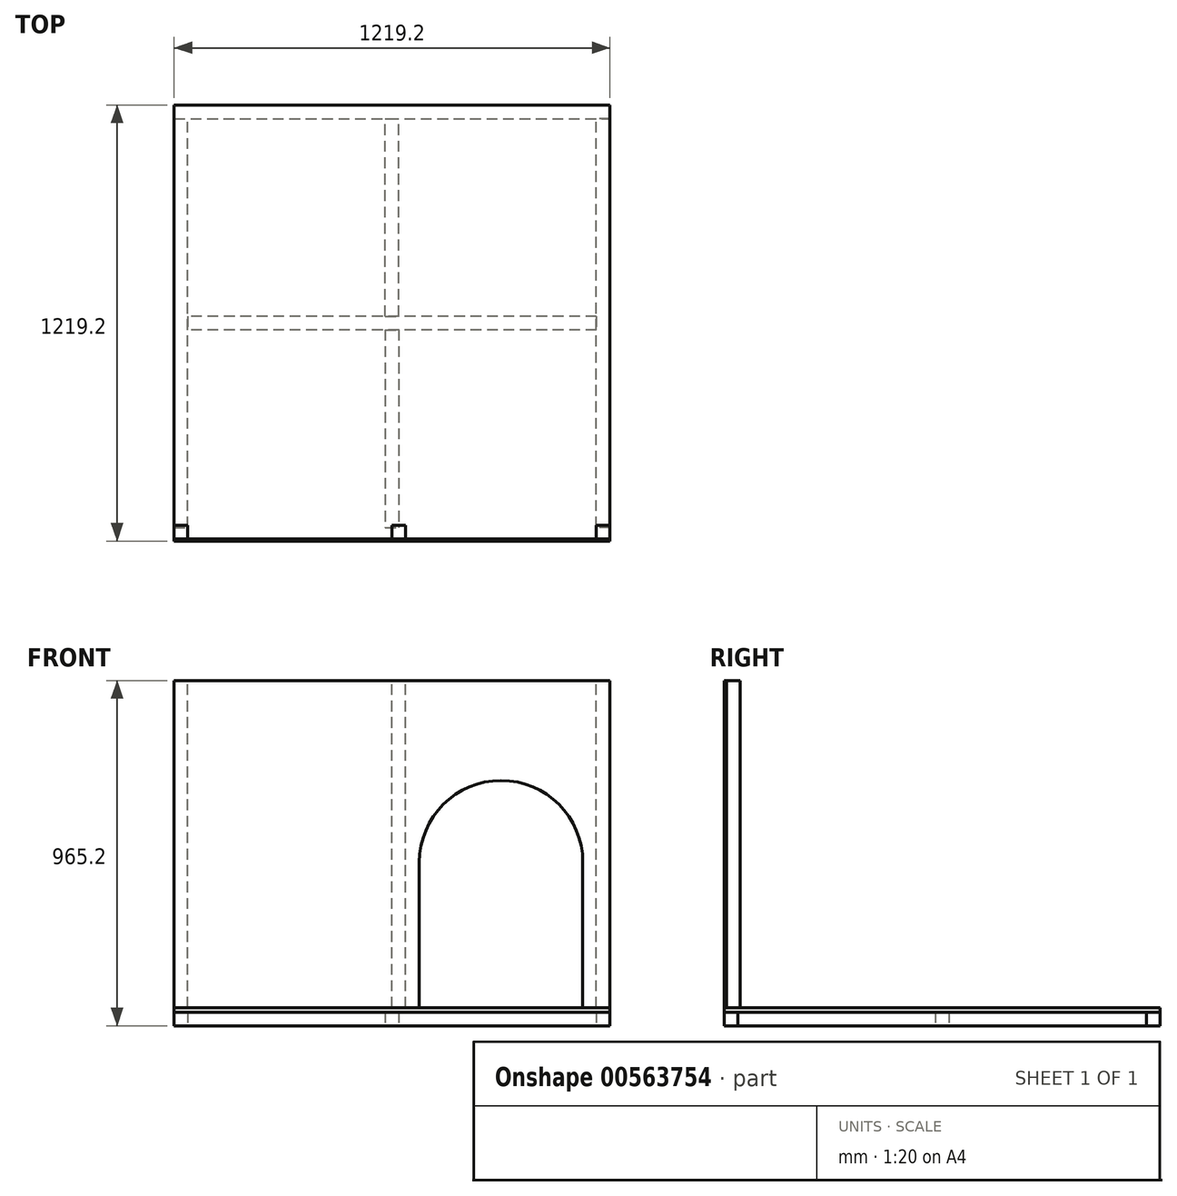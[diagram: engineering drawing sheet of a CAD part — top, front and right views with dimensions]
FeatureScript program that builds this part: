
annotation { "Feature Type Name" : "Feature", "Feature Type Description" : "" }
export const myFeature = defineFeature(function(context is Context, id is Id, definition is map)
    precondition{}
    {
        {
            var Q0;
            Q0=qCreatedBy(makeId("Top.planeOp"),FACE);
            var sketch = newSketch(context, id + "F0", { "sketchPlane" : qUnion([Q0])});
            skLineSegment(sketch, "E0.bottom", {"start": v(609.6, 609.6) * mm, "end": v(-609.6, 609.6) * mm, "construction": true});
            skLineSegment(sketch, "E0.top", {"start": v(609.6, -609.6) * mm, "end": v(-609.6, -609.6) * mm, "construction": true});
            skLineSegment(sketch, "E0.left", {"start": v(609.6, 609.6) * mm, "end": v(609.6, -609.6) * mm, "construction": true});
            skLineSegment(sketch, "E0.right", {"start": v(-609.6, 609.6) * mm, "end": v(-609.6, -609.6) * mm, "construction": true});
            skPoint(sketch, "E0.middle", {"position": v(0, 0) * mm});
            skSolve(sketch);
        }
        {
            var Q0;
            Q0=qCreatedBy(makeId("Top.planeOp"),FACE);
            var sketch = newSketch(context, id + "F1", { "sketchPlane" : qUnion([Q0])});
            skPoint(sketch, "E1.0", {"position": v(-609.6, -609.6) * mm});
            skLineSegment(sketch, "E2.bottom", {"start": v(-609.6, -609.6) * mm, "end": v(609.6, -609.6) * mm});
            skLineSegment(sketch, "E2.top", {"start": v(-609.6, -571.5) * mm, "end": v(609.6, -571.5) * mm});
            skLineSegment(sketch, "E2.left", {"start": v(-609.6, -609.6) * mm, "end": v(-609.6, -571.5) * mm});
            skLineSegment(sketch, "E2.right", {"start": v(609.6, -609.6) * mm, "end": v(609.6, -571.5) * mm});
            skPoint(sketch, "E3.0", {"position": v(-609.6, 609.6) * mm});
            skLineSegment(sketch, "E4.bottom", {"start": v(-609.6, 609.6) * mm, "end": v(609.6, 609.6) * mm});
            skLineSegment(sketch, "E4.top", {"start": v(-609.6, 571.5) * mm, "end": v(609.6, 571.5) * mm});
            skLineSegment(sketch, "E4.left", {"start": v(-609.6, 609.6) * mm, "end": v(-609.6, 571.5) * mm});
            skLineSegment(sketch, "E4.right", {"start": v(609.6, 609.6) * mm, "end": v(609.6, 571.5) * mm});
            skLineSegment(sketch, "E5.bottom", {"start": v(571.5, 19.05) * mm, "end": v(-571.5, 19.05) * mm});
            skLineSegment(sketch, "E5.top", {"start": v(571.5, -19.05) * mm, "end": v(-571.5, -19.05) * mm});
            skLineSegment(sketch, "E5.left", {"start": v(571.5, 19.05) * mm, "end": v(571.5, -19.05) * mm});
            skLineSegment(sketch, "E5.right", {"start": v(-571.5, 19.05) * mm, "end": v(-571.5, -19.05) * mm});
            skPoint(sketch, "E5.middle", {"position": v(0, 0) * mm});
            skSolve(sketch);
        }
        {
            var Q0;
            Q0 = qSketchRegion(id + "F1", true);
            extrude(context, id + "F2", {"entities" : qUnion([Q0]), "depth" : 38.1 * mm, "offsetDistance" : 25.4 * mm});
        }
        {
            var Q0;
            Q0=qCreatedBy(makeId("Top.planeOp"),FACE);
            var sketch = newSketch(context, id + "F3", { "sketchPlane" : qUnion([Q0])});
            skPoint(sketch, "E6.0", {"position": v(609.6, 0) * mm});
            skPoint(sketch, "E7.0", {"position": v(-609.6, 0) * mm});
            skPoint(sketch, "E8.0", {"position": v(609.6, -609.6) * mm});
            skLineSegment(sketch, "E9", {"start": v(609.6, -609.6) * mm, "end": v(609.6, -571.5) * mm, "construction": true});
            skLineSegment(sketch, "E10.bottom", {"start": v(609.6, -571.5) * mm, "end": v(571.5, -571.5) * mm});
            skLineSegment(sketch, "E10.top", {"start": v(609.6, 571.5) * mm, "end": v(571.5, 571.5) * mm});
            skLineSegment(sketch, "E10.left", {"start": v(609.6, -571.5) * mm, "end": v(609.6, 571.5) * mm});
            skLineSegment(sketch, "E10.right", {"start": v(571.5, -571.5) * mm, "end": v(571.5, 571.5) * mm});
            skLineSegment(sketch, "E11.MirrorCS", {"start": v(-571.5, -571.5) * mm, "end": v(-571.5, 571.5) * mm});
            skLineSegment(sketch, "E12.MirrorCS", {"start": v(-609.6, -571.5) * mm, "end": v(-609.6, 571.5) * mm});
            skLineSegment(sketch, "E13.MirrorCS", {"start": v(-609.6, 571.5) * mm, "end": v(-571.5, 571.5) * mm});
            skLineSegment(sketch, "E14.MirrorCS", {"start": v(-609.6, -571.5) * mm, "end": v(-571.5, -571.5) * mm});
            skSolve(sketch);
        }
        {
            var Q0;
            Q0 = qSketchRegion(id + "F3", true);
            extrude(context, id + "F4", {"entities" : qUnion([Q0]), "depth" : 38.1 * mm, "offsetDistance" : 25.4 * mm});
        }
        {
            var Q0;
            Q0=qCreatedBy(makeId("Top.planeOp"),FACE);
            var sketch = newSketch(context, id + "F5", { "sketchPlane" : qUnion([Q0])});
            skLineSegment(sketch, "E15", {"start": v(0, 19.05) * mm, "end": v(0, -19.05) * mm, "construction": true});
            skLineSegment(sketch, "E16.bottom", {"start": v(-19.05, 19.05) * mm, "end": v(19.05, 19.05) * mm});
            skLineSegment(sketch, "E16.top", {"start": v(-19.05, 571.5) * mm, "end": v(19.05, 571.5) * mm});
            skLineSegment(sketch, "E16.left", {"start": v(-19.05, 19.05) * mm, "end": v(-19.05, 571.5) * mm});
            skLineSegment(sketch, "E16.right", {"start": v(19.05, 19.05) * mm, "end": v(19.05, 571.5) * mm});
            skLineSegment(sketch, "E17.MirrorCS", {"start": v(19.05, -19.05) * mm, "end": v(19.05, -571.5) * mm});
            skLineSegment(sketch, "E18.MirrorCS", {"start": v(-19.05, -19.05) * mm, "end": v(-19.05, -571.5) * mm});
            skLineSegment(sketch, "E19.MirrorCS", {"start": v(-19.05, -19.05) * mm, "end": v(19.05, -19.05) * mm});
            skLineSegment(sketch, "E20.MirrorCS", {"start": v(-19.05, -571.5) * mm, "end": v(19.05, -571.5) * mm});
            skSolve(sketch);
        }
        {
            var Q0;
            Q0 = qSketchRegion(id + "F5", true);
            extrude(context, id + "F6", {"entities" : qUnion([Q0]), "depth" : 38.1 * mm, "offsetDistance" : 25.4 * mm});
        }
        {
            var Q0;
            Q0=makeQuery(id+"F2.opExtrude","CAP_FACE",FACE,{"disambiguationData":[OSD([sQuery(id+"F1.wireOp",EDGE,"E4.bottom"),sQuery(id+"F1.wireOp",EDGE,"E4.top"),sQuery(id+"F1.wireOp",EDGE,"E4.left"),sQuery(id+"F1.wireOp",EDGE,"E4.right")])],"isStart":false});
            var sketch = newSketch(context, id + "F7", { "sketchPlane" : qUnion([Q0])});
            skPoint(sketch, "E21.0", {"position": v(609.6, -609.6) * mm});
            skPoint(sketch, "E22.0", {"position": v(-609.6, 609.6) * mm});
            skLineSegment(sketch, "E23.bottom", {"start": v(609.6, -609.6) * mm, "end": v(-609.6, -609.6) * mm});
            skLineSegment(sketch, "E23.top", {"start": v(609.6, 609.6) * mm, "end": v(-609.6, 609.6) * mm});
            skLineSegment(sketch, "E23.left", {"start": v(609.6, -609.6) * mm, "end": v(609.6, 609.6) * mm});
            skLineSegment(sketch, "E23.right", {"start": v(-609.6, -609.6) * mm, "end": v(-609.6, 609.6) * mm});
            skSolve(sketch);
        }
        {
            var Q0;
            Q0 = qSketchRegion(id + "F7", true);
            extrude(context, id + "F8", {"entities" : qUnion([Q0]), "depth" : 12.7 * mm, "offsetDistance" : 25.4 * mm});
        }
        {
            var Q0;
            Q0=makeQuery(id+"F8.opExtrude","SWEPT_FACE",FACE,{"disambiguationData":[OSD([sQuery(id+"F7.wireOp",EDGE,"E23.bottom")])]});
            var sketch = newSketch(context, id + "F9", { "sketchPlane" : qUnion([Q0])});
            skPoint(sketch, "E24.0", {"position": v(-609.6, 50.8) * mm});
            skPoint(sketch, "E25.0", {"position": v(609.6, 50.8) * mm});
            skLineSegment(sketch, "E26.bottom", {"start": v(-609.6, 50.8) * mm, "end": v(609.6, 50.8) * mm});
            skLineSegment(sketch, "E26.top", {"start": v(-609.6, 965.2) * mm, "end": v(609.6, 965.2) * mm});
            skLineSegment(sketch, "E26.left", {"start": v(-609.6, 50.8) * mm, "end": v(-609.6, 965.2) * mm});
            skLineSegment(sketch, "E26.right", {"start": v(609.6, 50.8) * mm, "end": v(609.6, 965.2) * mm});
            skSolve(sketch);
        }
        {
            var Q0;
            Q0 = qSketchRegion(id + "F9", true);
            extrude(context, id + "F10", {"entities" : qUnion([Q0]), "oppositeDirection" : true, "depth" : 6.35 * mm, "offsetDistance" : 25.4 * mm});
        }
        {
            var Q0;
            Q0=makeQuery(id+"F10.boolean.opBoolean","MERGE",FACE,{"derivedFrom":[makeQuery(id+"F8.opExtrude","SWEPT_FACE",FACE,{"disambiguationData":[OSD([sQuery(id+"F7.wireOp",EDGE,"E23.bottom")])]}),makeQuery(id+"F10.opExtrude","CAP_FACE",FACE,{"disambiguationData":[OSD([sQuery(id+"F9.wireOp",EDGE,"E26.bottom"),sQuery(id+"F9.wireOp",EDGE,"E26.top"),sQuery(id+"F9.wireOp",EDGE,"E26.left"),sQuery(id+"F9.wireOp",EDGE,"E26.right")])],"isStart":true})]});
            var sketch = newSketch(context, id + "F11", { "sketchPlane" : qUnion([Q0])});
            skLineSegment(sketch, "E27.0", {"start": v(-609.6, 965.2) * mm, "end": v(609.6, 965.2) * mm, "construction": true});
            skLineSegment(sketch, "E28.0", {"start": v(609.6, 965.2) * mm, "end": v(609.6, 38.1) * mm, "construction": true});
            skLineSegment(sketch, "E29.0", {"start": v(-609.6, 38.1) * mm, "end": v(76.2, 38.1) * mm, "construction": true});
            skLineSegment(sketch, "E30.0", {"start": v(-609.6, 965.2) * mm, "end": v(-609.6, 38.1) * mm, "construction": true});
            skLineSegment(sketch, "E31", {"start": v(0, 965.2) * mm, "end": v(0, 38.1) * mm, "construction": true});
            skLineSegment(sketch, "E32.top", {"start": v(-533.4, 38.1) * mm, "end": v(-76.2, 38.1) * mm});
            skLineSegment(sketch, "E33.top", {"start": v(76.2, 38.1) * mm, "end": v(533.4, 38.1) * mm});
            skPoint(sketch, "E34", {"position": v(76.2, 50.8) * mm});
            skPoint(sketch, "E35", {"position": v(533.4, 50.8) * mm});
            skLineSegment(sketch, "E36", {"start": v(76.2, 50.8) * mm, "end": v(533.4, 50.8) * mm});
            skPoint(sketch, "E37.trimOffspring.end.orphan", {"position": v(609.6, 38.1) * mm});
            skLineSegment(sketch, "E38.left", {"start": v(76.2, 50.8) * mm, "end": v(76.2, 457.2) * mm});
            skLineSegment(sketch, "E38.right", {"start": v(533.4, 50.8) * mm, "end": v(533.4, 457.2) * mm});
            skArc(sketch, "E39", {"start": v(533.4, 457.2) * mm, "mid": v(304.8, 685.8) * mm, "end": v(76.2, 457.2) * mm});
            skSolve(sketch);
        }
        {
            var Q0;
            Q0 = qSketchRegion(id + "F11", true);
            extrude(context, id + "F12", {"entities" : qUnion([Q0]), "operationType" : NewBodyOperationType.REMOVE, "oppositeDirection" : true, "depth" : 254 * mm, "offsetDistance" : 25.4 * mm});
        }
        {
            var Q0;
            Q0=makeQuery(id+"F10.opExtrude","CAP_FACE",FACE,{"disambiguationData":[OSD([sQuery(id+"F9.wireOp",EDGE,"E26.bottom"),sQuery(id+"F9.wireOp",EDGE,"E26.top"),sQuery(id+"F9.wireOp",EDGE,"E26.left"),sQuery(id+"F9.wireOp",EDGE,"E26.right")])],"isStart":false});
            var sketch = newSketch(context, id + "F13", { "sketchPlane" : qUnion([Q0])});
            skLineSegment(sketch, "E40.bottom", {"start": v(-609.6, 50.8) * mm, "end": v(-571.5, 50.8) * mm});
            skLineSegment(sketch, "E40.top", {"start": v(-609.6, 965.2) * mm, "end": v(-571.5, 965.2) * mm});
            skLineSegment(sketch, "E40.left", {"start": v(-609.6, 50.8) * mm, "end": v(-609.6, 965.2) * mm});
            skLineSegment(sketch, "E40.right", {"start": v(-571.5, 50.8) * mm, "end": v(-571.5, 965.2) * mm});
            skLineSegment(sketch, "E41.bottom", {"start": v(609.6, 50.8) * mm, "end": v(571.5, 50.8) * mm});
            skLineSegment(sketch, "E41.top", {"start": v(609.6, 965.2) * mm, "end": v(571.5, 965.2) * mm});
            skLineSegment(sketch, "E41.left", {"start": v(609.6, 50.8) * mm, "end": v(609.6, 965.2) * mm});
            skLineSegment(sketch, "E41.right", {"start": v(571.5, 50.8) * mm, "end": v(571.5, 965.2) * mm});
            skSolve(sketch);
        }
        {
            var Q0;
            Q0 = qSketchRegion(id + "F13", true);
            extrude(context, id + "F14", {"entities" : qUnion([Q0]), "depth" : 38.1 * mm, "offsetDistance" : 25.4 * mm});
        }
        {
            var Q0;
            Q0=makeQuery(id+"F10.opExtrude","CAP_FACE",FACE,{"disambiguationData":[OSD([sQuery(id+"F9.wireOp",EDGE,"E26.bottom"),sQuery(id+"F9.wireOp",EDGE,"E26.top"),sQuery(id+"F9.wireOp",EDGE,"E26.left"),sQuery(id+"F9.wireOp",EDGE,"E26.right")])],"isStart":false});
            var sketch = newSketch(context, id + "F15", { "sketchPlane" : qUnion([Q0])});
            skLineSegment(sketch, "E42.bottom", {"start": v(-76.2, 50.8) * mm, "end": v(0, 50.8) * mm, "construction": true});
            skLineSegment(sketch, "E42.top", {"start": v(-76.2, 50.8) * mm, "end": v(0, 50.8) * mm, "construction": true});
            skLineSegment(sketch, "E42.left", {"start": v(-76.2, 50.8) * mm, "end": v(-76.2, 50.8) * mm});
            skLineSegment(sketch, "E42.right", {"start": v(0, 50.8) * mm, "end": v(0, 50.8) * mm});
            skLineSegment(sketch, "E43", {"start": v(-76.2, 50.8) * mm, "end": v(-38.1, 50.8) * mm, "construction": true});
            skLineSegment(sketch, "E44.bottom", {"start": v(-38.1, 50.8) * mm, "end": v(0, 50.8) * mm});
            skLineSegment(sketch, "E44.top", {"start": v(-38.1, 965.2) * mm, "end": v(0, 965.2) * mm});
            skLineSegment(sketch, "E44.left", {"start": v(-38.1, 50.8) * mm, "end": v(-38.1, 965.2) * mm});
            skLineSegment(sketch, "E44.right", {"start": v(0, 50.8) * mm, "end": v(0, 965.2) * mm});
            skSolve(sketch);
        }
        {
            var Q0;
            Q0 = qSketchRegion(id + "F15", true);
            extrude(context, id + "F16", {"entities" : qUnion([Q0]), "depth" : 38.1 * mm, "offsetDistance" : 25.4 * mm});
        }
    });
